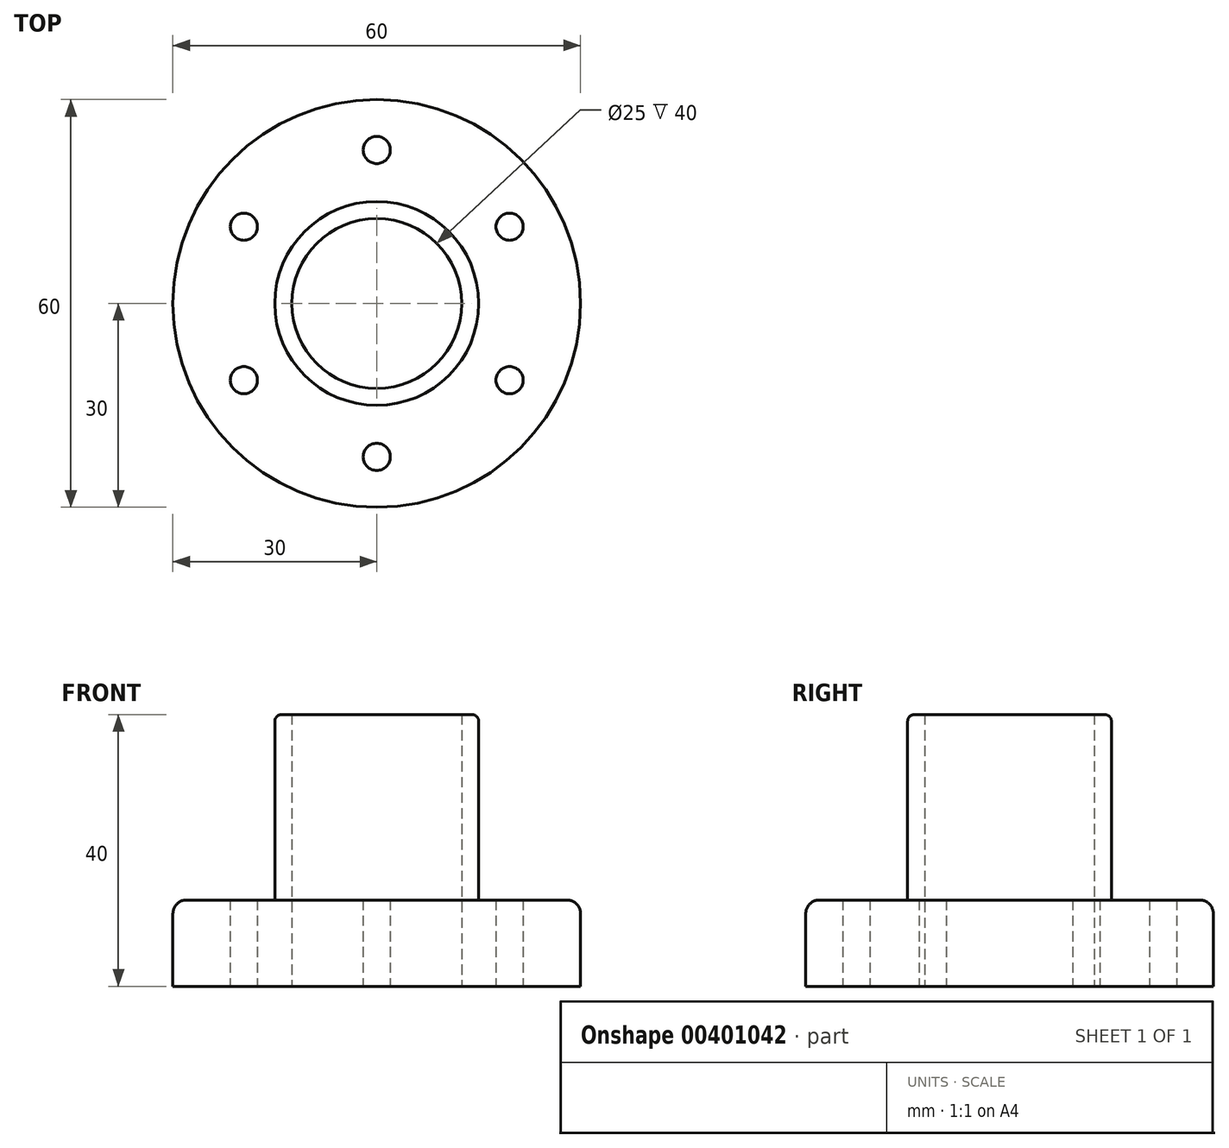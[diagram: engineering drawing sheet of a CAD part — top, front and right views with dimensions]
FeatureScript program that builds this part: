
annotation { "Feature Type Name" : "Feature", "Feature Type Description" : "" }
export const myFeature = defineFeature(function(context is Context, id is Id, definition is map)
    precondition{}
    {
        {
            var Q0;
            Q0=qCreatedBy(makeId("Top.planeOp"),FACE);
            var sketch = newSketch(context, id + "F0", { "sketchPlane" : qUnion([Q0])});
            skCircle(sketch, "E0", {"center": v(0, 0) * mm, "radius": 15 * mm});
            skCircle(sketch, "E1", {"center": v(0, 22.58) * mm, "radius": 2 * mm});
            skCircle(sketch, "E2.1.0", {"center": v(-19.56, 11.3) * mm, "radius": 2 * mm});
            skCircle(sketch, "E2.2.0", {"center": v(-19.56, -11.3) * mm, "radius": 2 * mm});
            skCircle(sketch, "E2.3.0", {"center": v(0, -22.58) * mm, "radius": 2 * mm});
            skCircle(sketch, "E2.4.0", {"center": v(19.56, -11.3) * mm, "radius": 2 * mm});
            skCircle(sketch, "E2.5.0", {"center": v(19.56, 11.3) * mm, "radius": 2 * mm});
            skCircle(sketch, "E3", {"center": v(0, 0) * mm, "radius": 12.5 * mm});
            skCircle(sketch, "E4", {"center": v(0, 0) * mm, "radius": 30 * mm});
            skSolve(sketch);
        }
        {
            var Q0;
            Q0=makeQuery(id+"F0.imprint","IMPRINT",FACE,{"disambiguationData":[TD([[makeQuery(id+"F0.imprint","IMPRINT",EDGE,{"derivedFrom":sQuery(id+"F0.wireOp",EDGE,"E0")}),1.0]])]});
            var Q1;
            Q1=makeQuery(id+"F0.imprint","IMPRINT",FACE,{"disambiguationData":[TD([[makeQuery(id+"F0.imprint","IMPRINT",EDGE,{"derivedFrom":sQuery(id+"F0.wireOp",EDGE,"E0")}),-1.0]])]});
            extrude(context, id + "F1", {"entities" : qUnion([Q0, Q1]), "depth" : 12.7 * mm});
        }
        {
            var Q0;
            Q0=makeQuery(id+"F0.imprint","IMPRINT",FACE,{"disambiguationData":[TD([[makeQuery(id+"F0.imprint","IMPRINT",EDGE,{"derivedFrom":sQuery(id+"F0.wireOp",EDGE,"E0")}),1.0]])]});
            extrude(context, id + "F2", {"entities" : qUnion([Q0]), "operationType" : NewBodyOperationType.ADD, "depth" : 40 * mm});
        }
        {
            var Q0;
            Q0=makeQuery(id+"F2.opExtrude","CAP_EDGE",EDGE,{"disambiguationData":[OSD([sQuery(id+"F0.wireOp",EDGE,"E0")])],"isStart":false});
            fillet(context, id + "F3", {"entities" : qUnion([Q0]), "radius" : 1 * mm, "tangentPropagation" : true, "allowEdgeOverflow" : false});
        }
        {
            var Q0;
            Q0=makeQuery(id+"F1.opExtrude","CAP_EDGE",EDGE,{"disambiguationData":[OSD([sQuery(id+"F0.wireOp",EDGE,"E4")])],"isStart":false});
            fillet(context, id + "F4", {"entities" : qUnion([Q0]), "radius" : 2 * mm, "tangentPropagation" : true, "allowEdgeOverflow" : false});
        }
    });
